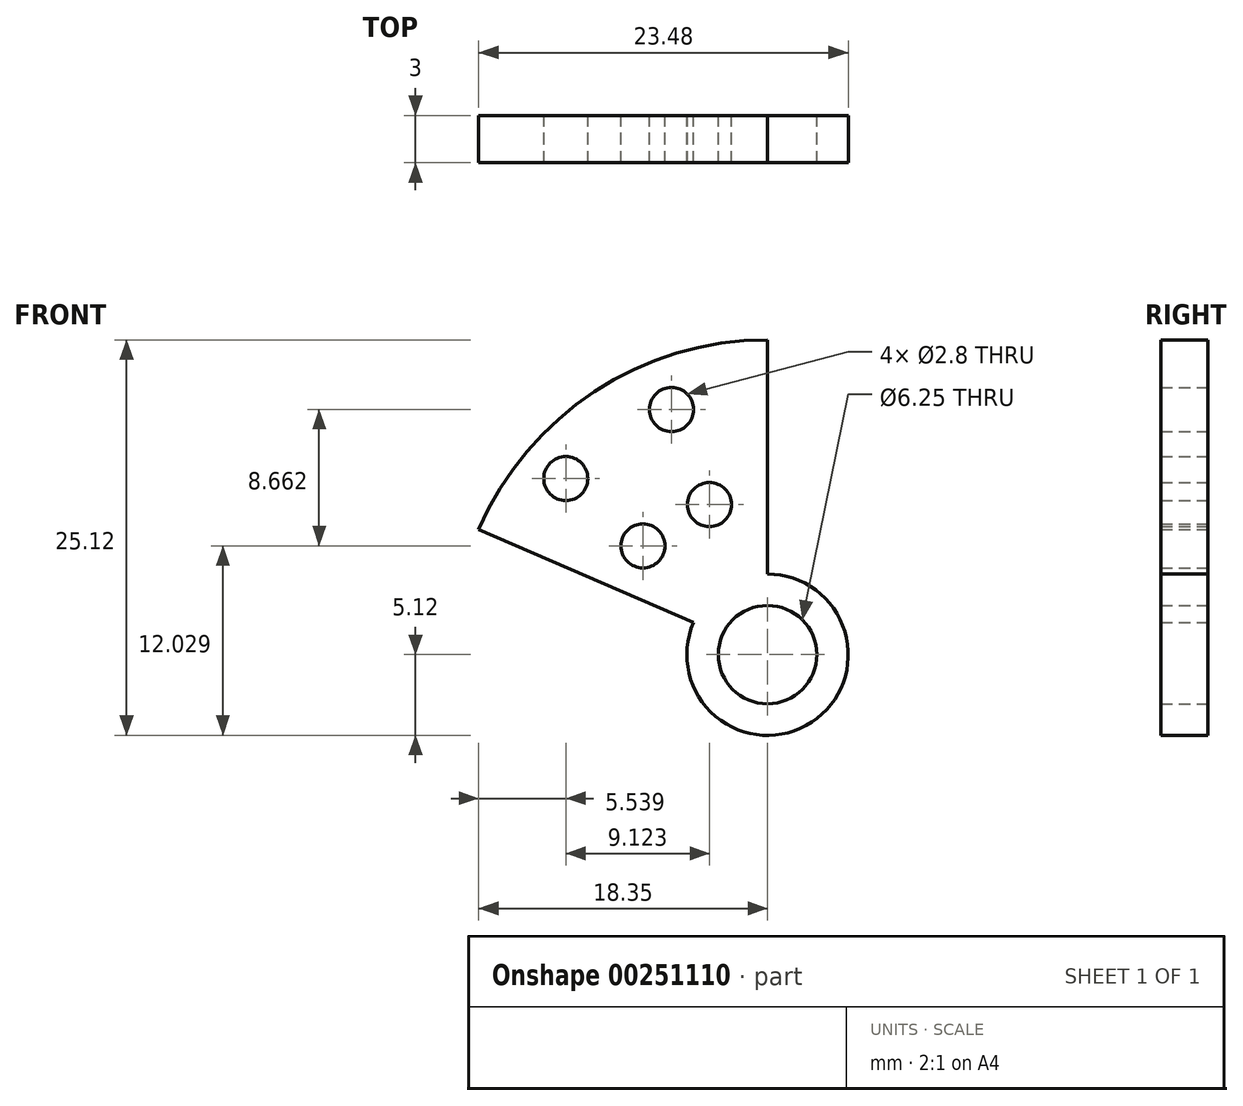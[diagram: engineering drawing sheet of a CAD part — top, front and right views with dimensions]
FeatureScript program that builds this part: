
annotation { "Feature Type Name" : "Feature", "Feature Type Description" : "" }
export const myFeature = defineFeature(function(context is Context, id is Id, definition is map)
    precondition{}
    {
        {
            var Q0;
            Q0=qCreatedBy(makeId("Front.planeOp"),FACE);
            var sketch = newSketch(context, id + "F0", { "sketchPlane" : qUnion([Q0])});
            skCircle(sketch, "E0", {"center": v(0, 0) * mm, "radius": 3.12 * mm});
            skCircle(sketch, "E1", {"center": v(0, 0) * mm, "radius": 20 * mm});
            skLineSegment(sketch, "E2", {"start": v(-3.12, 0) * mm, "end": v(-20, 0) * mm});
            skLineSegment(sketch, "E3", {"start": v(0, 0) * mm, "end": v(0, 20) * mm});
            skLineSegment(sketch, "E4.1.0", {"start": v(0, 0) * mm, "end": v(-15.07, 13.15) * mm, "construction": true});
            skLineSegment(sketch, "E4.2.0", {"start": v(0, 0) * mm, "end": v(-7.3, 18.62) * mm, "construction": true});
            skLineSegment(sketch, "E4.anchor2", {"start": v(0, 0) * mm, "end": v(-7.3, 18.62) * mm, "construction": true});
            skCircle(sketch, "E5", {"center": v(-10.4, 2.52) * mm, "radius": 1.4 * mm});
            skCircle(sketch, "E6.1.0", {"center": v(-7.91, 6.9) * mm, "radius": 1.4 * mm});
            skCircle(sketch, "E6.2.0", {"center": v(-3.69, 9.53) * mm, "radius": 1.4 * mm});
            skPoint(sketch, "E6.center", {"position": v(0.05, -0.01) * mm});
            skLineSegment(sketch, "E6.anchor1", {"start": v(0.05, -0.01) * mm, "end": v(-10.4, 2.52) * mm, "construction": true});
            skLineSegment(sketch, "E6.anchor2", {"start": v(0.05, -0.01) * mm, "end": v(-3.69, 9.53) * mm, "construction": true});
            skCircle(sketch, "E7.0", {"center": v(0, 0) * mm, "radius": 5.13 * mm});
            skCircle(sketch, "E8", {"center": v(-12.81, 11.18) * mm, "radius": 1.4 * mm});
            skCircle(sketch, "E9", {"center": v(-6.1, 15.57) * mm, "radius": 1.4 * mm});
            skLineSegment(sketch, "E10", {"start": v(0.05, -0.01) * mm, "end": v(-18.84, 8.16) * mm});
            skSolve(sketch);
        }
        {
            var Q0;
            {var subQ0=sQuery(id+"F0.wireOp",EDGE,"E2");Q0=makeQuery(id+"F0.imprint","IMPRINT",FACE,{"disambiguationData":[TD([[makeQuery(id+"F0.imprint","IMPRINT",EDGE,{"derivedFrom":subQ0}),-1.0]])]});}
            var Q1;
            Q1=makeQuery(id+"F0.imprint","IMPRINT",FACE,{"disambiguationData":[TD([[makeQuery(id+"F0.imprint","IMPRINT",EDGE,{"derivedFrom":sQuery(id+"F0.wireOp",EDGE,"xl4TGOYK-pVOm-mxPA-wxaf-5OBtAY3ibSXa")}),-1.0]])]});
            var Q2;
            {var subQ0=sQuery(id+"F0.wireOp",EDGE,"E2");var subQ1=sQuery(id+"F0.wireOp",EDGE,"E0");var subQ2=makeQuery(id+"F0.imprint","INTERSECT",VERTEX,{"derivedFrom":[subQ1,subQ0]});Q2=makeQuery(id+"F0.imprint","IMPRINT",FACE,{"disambiguationData":[TD([[makeQuery(id+"F0.imprint","IMPRINT",EDGE,{"disambiguationData":[TD([[subQ2,-1.0]])],"derivedFrom":subQ1}),-1.0]])]});}
            var Q3;
            Q3=makeQuery(id+"F0.imprint","IMPRINT",FACE,{"disambiguationData":[TD([[makeQuery(id+"F0.imprint","IMPRINT",EDGE,{"derivedFrom":sQuery(id+"F0.wireOp",EDGE,"E6.1.0")}),-1.0]])]});
            var Q4;
            {var subQ0=sQuery(id+"F0.wireOp",EDGE,"E10");var subQ1=sQuery(id+"F0.wireOp",EDGE,"E0");var subQ2=makeQuery(id+"F0.imprint","INTERSECT",VERTEX,{"derivedFrom":[subQ1,subQ0]});Q4=makeQuery(id+"F0.imprint","IMPRINT",FACE,{"disambiguationData":[TD([[makeQuery(id+"F0.imprint","IMPRINT",EDGE,{"disambiguationData":[TD([[subQ2,1.0]])],"derivedFrom":subQ1}),-1.0]])]});}
            extrude(context, id + "F1", {"entities" : qUnion([Q0, Q1, Q2, Q3, Q4]), "depth" : 3 * mm});
        }
    });
